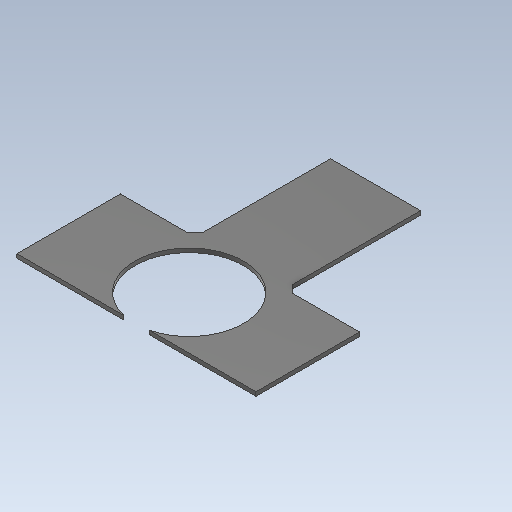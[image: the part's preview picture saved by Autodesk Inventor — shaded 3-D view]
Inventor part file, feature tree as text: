
AUTODESK INVENTOR PART (.ipt)
format: ipt  version: 2020 (Build 240168000, 168)  size: 124,416 bytes
history: native  units: in
note: dims shown in document units (in); Inventor stores cm internally (conversion verified against a paired STEP export)
features: extrude x1, sketch x1
ambient origin geometry x8: Origin, YZ Plane, XZ Plane, XY Plane, X Axis, Y Axis, Z Axis, Center Point
bodies: Solid1 (feature_tree)
feature tree (2):
  extrude  "Extrusion1"  Depth=3.8189in
  sketch  "Sketch2"  dims[d1=1.7323in d2=3.8189in d3=3.8189in d4=1.9094in d5=1.9094in d7=1.067in d8=1.1909in d9=1.1909in d10=2.1654in d11=2.1654in d12=0.063in d13=0.0in d14=0.0in d15=45.0deg d16=0.1181in d17=0.1181in]
